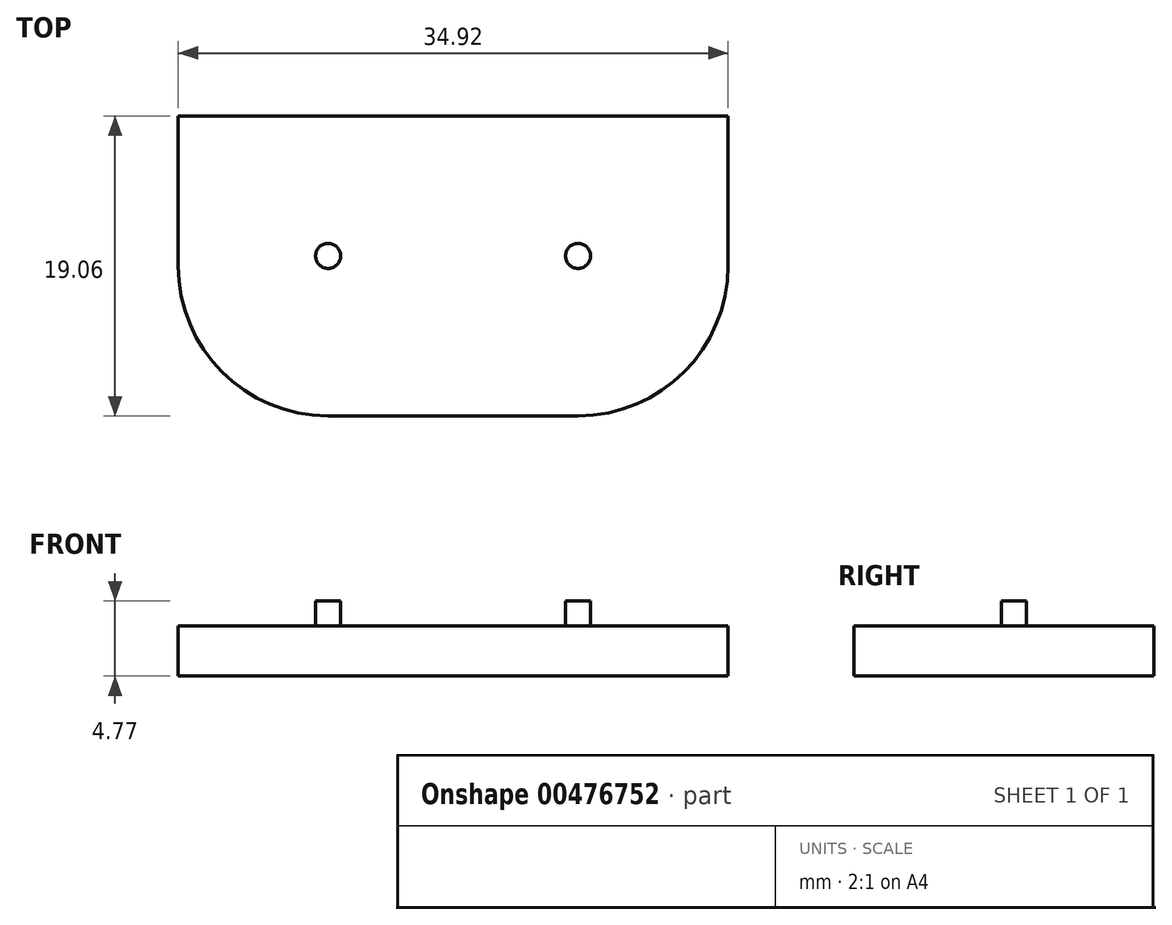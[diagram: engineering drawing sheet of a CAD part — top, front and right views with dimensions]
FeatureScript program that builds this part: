
annotation { "Feature Type Name" : "Feature", "Feature Type Description" : "" }
export const myFeature = defineFeature(function(context is Context, id is Id, definition is map)
    precondition{}
    {
        {
            var Q0;
            Q0=qCreatedBy(makeId("Top.planeOp"),FACE);
            var sketch = newSketch(context, id + "F0", { "sketchPlane" : qUnion([Q0])});
            skLineSegment(sketch, "E0.bottom", {"start": v(17.46, -9.53) * mm, "end": v(-17.46, -9.53) * mm});
            skLineSegment(sketch, "E0.top", {"start": v(17.46, 9.53) * mm, "end": v(-17.46, 9.53) * mm});
            skLineSegment(sketch, "E0.left", {"start": v(17.46, -9.53) * mm, "end": v(17.46, 9.53) * mm});
            skLineSegment(sketch, "E0.right", {"start": v(-17.46, -9.53) * mm, "end": v(-17.46, 9.52) * mm});
            skPoint(sketch, "E0.middle", {"position": v(0, 0) * mm});
            skCircle(sketch, "E1", {"center": v(-7.94, 0.64) * mm, "radius": 0.8 * mm});
            skCircle(sketch, "E2", {"center": v(7.94, 0.64) * mm, "radius": 0.8 * mm});
            skSolve(sketch);
        }
        {
            var Q0;
            Q0=makeQuery(id+"F0.imprint","IMPRINT",FACE,{"disambiguationData":[TD([[makeQuery(id+"F0.imprint","IMPRINT",EDGE,{"derivedFrom":sQuery(id+"F0.wireOp",EDGE,"E0.bottom")}),-1.0]])]});
            var Q1;
            Q1=makeQuery(id+"F0.imprint","IMPRINT",FACE,{"disambiguationData":[TD([[makeQuery(id+"F0.imprint","IMPRINT",EDGE,{"derivedFrom":sQuery(id+"F0.wireOp",EDGE,"E1")}),1.0]])]});
            var Q2;
            Q2=makeQuery(id+"F0.imprint","IMPRINT",FACE,{"disambiguationData":[TD([[makeQuery(id+"F0.imprint","IMPRINT",EDGE,{"derivedFrom":sQuery(id+"F0.wireOp",EDGE,"E2")}),1.0]])]});
            extrude(context, id + "F1", {"entities" : qUnion([Q0, Q1, Q2]), "depth" : 3.17 * mm, "symmetric" : true});
        }
        {
            var Q0;
            Q0=makeQuery(id+"F0.imprint","IMPRINT",FACE,{"disambiguationData":[TD([[makeQuery(id+"F0.imprint","IMPRINT",EDGE,{"derivedFrom":sQuery(id+"F0.wireOp",EDGE,"E1")}),1.0]])]});
            var Q1;
            Q1=makeQuery(id+"F0.imprint","IMPRINT",FACE,{"disambiguationData":[TD([[makeQuery(id+"F0.imprint","IMPRINT",EDGE,{"derivedFrom":sQuery(id+"F0.wireOp",EDGE,"E2")}),1.0]])]});
            extrude(context, id + "F2", {"entities" : qUnion([Q0, Q1]), "operationType" : NewBodyOperationType.ADD, "depth" : 3.17 * mm});
        }
        {
            var Q0;
            Q0=makeQuery(id+"F1.opExtrude","SWEPT_EDGE",EDGE,{"disambiguationData":[OSD([sQuery(id+"F0.wireOp",EDGE,"E0.bottom"),sQuery(id+"F0.wireOp",EDGE,"E0.left")])]});
            var Q1;
            Q1=makeQuery(id+"F1.opExtrude","SWEPT_EDGE",EDGE,{"disambiguationData":[OSD([sQuery(id+"F0.wireOp",EDGE,"E0.bottom"),sQuery(id+"F0.wireOp",EDGE,"E0.right")])]});
            fillet(context, id + "F3", {"entities" : qUnion([Q0, Q1]), "radius" : 9.52 * mm, "tangentPropagation" : true, "allowEdgeOverflow" : false});
        }
    });
